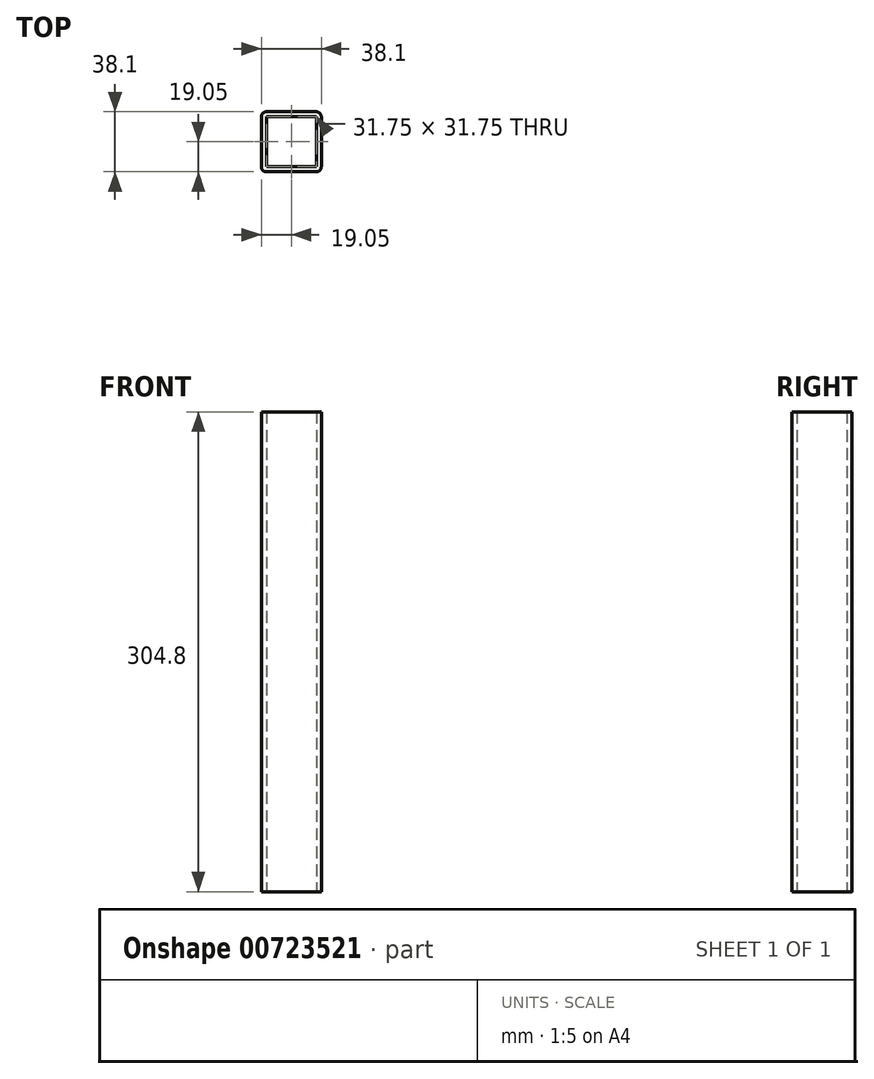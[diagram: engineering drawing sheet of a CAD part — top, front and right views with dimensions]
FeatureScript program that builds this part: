
annotation { "Feature Type Name" : "Feature", "Feature Type Description" : "" }
export const myFeature = defineFeature(function(context is Context, id is Id, definition is map)
    precondition{}
    {
        {
            var Q0;
            Q0=qCreatedBy(makeId("Top.planeOp"),FACE);
            var sketch = newSketch(context, id + "F0", { "sketchPlane" : qUnion([Q0])});
            skLineSegment(sketch, "E0.bottom", {"start": v(-15.87, 19.05) * mm, "end": v(15.88, 19.05) * mm});
            skLineSegment(sketch, "E0.top", {"start": v(-15.87, -19.05) * mm, "end": v(15.87, -19.05) * mm});
            skLineSegment(sketch, "E0.left", {"start": v(-19.05, 15.87) * mm, "end": v(-19.05, -15.87) * mm});
            skLineSegment(sketch, "E0.right", {"start": v(19.05, 15.87) * mm, "end": v(19.05, -15.87) * mm});
            skPoint(sketch, "E1", {"position": v(0, 19.05) * mm});
            skPoint(sketch, "E2", {"position": v(-19.05, 0) * mm});
            skPoint(sketch, "E3.visualSharp", {"position": v(-19.05, 19.05) * mm});
            skArc(sketch, "E3.filletArc", {"start": v(-15.87, 19.05) * mm, "mid": v(-18.12, 18.12) * mm, "end": v(-19.05, 15.87) * mm});
            skPoint(sketch, "E4.visualSharp", {"position": v(19.05, 19.05) * mm});
            skArc(sketch, "E4.filletArc", {"start": v(19.05, 15.87) * mm, "mid": v(18.12, 18.12) * mm, "end": v(15.87, 19.05) * mm});
            skPoint(sketch, "E5.visualSharp", {"position": v(19.05, -19.05) * mm});
            skArc(sketch, "E5.filletArc", {"start": v(15.87, -19.05) * mm, "mid": v(18.12, -18.12) * mm, "end": v(19.05, -15.87) * mm});
            skPoint(sketch, "E6.visualSharp", {"position": v(-19.05, -19.05) * mm});
            skArc(sketch, "E6.filletArc", {"start": v(-19.05, -15.87) * mm, "mid": v(-18.12, -18.12) * mm, "end": v(-15.87, -19.05) * mm});
            skLineSegment(sketch, "E7.0", {"start": v(-15.87, 15.87) * mm, "end": v(15.87, 15.87) * mm});
            skLineSegment(sketch, "E7.1", {"start": v(-15.87, 15.88) * mm, "end": v(-15.87, -15.88) * mm});
            skLineSegment(sketch, "E7.2", {"start": v(-15.87, -15.87) * mm, "end": v(15.87, -15.87) * mm});
            skLineSegment(sketch, "E7.3", {"start": v(15.87, 15.88) * mm, "end": v(15.87, -15.88) * mm});
            skSolve(sketch);
        }
        {
            var Q0;
            Q0=makeQuery(id+"F0.imprint","IMPRINT",FACE,{"disambiguationData":[TD([[makeQuery(id+"F0.imprint","IMPRINT",EDGE,{"derivedFrom":sQuery(id+"F0.wireOp",EDGE,"E0.bottom")}),-1.0]])]});
            extrude(context, id + "F1", {"entities" : qUnion([Q0]), "depth" : 304.8 * mm, "offsetDistance" : 25.4 * mm});
        }
    });
